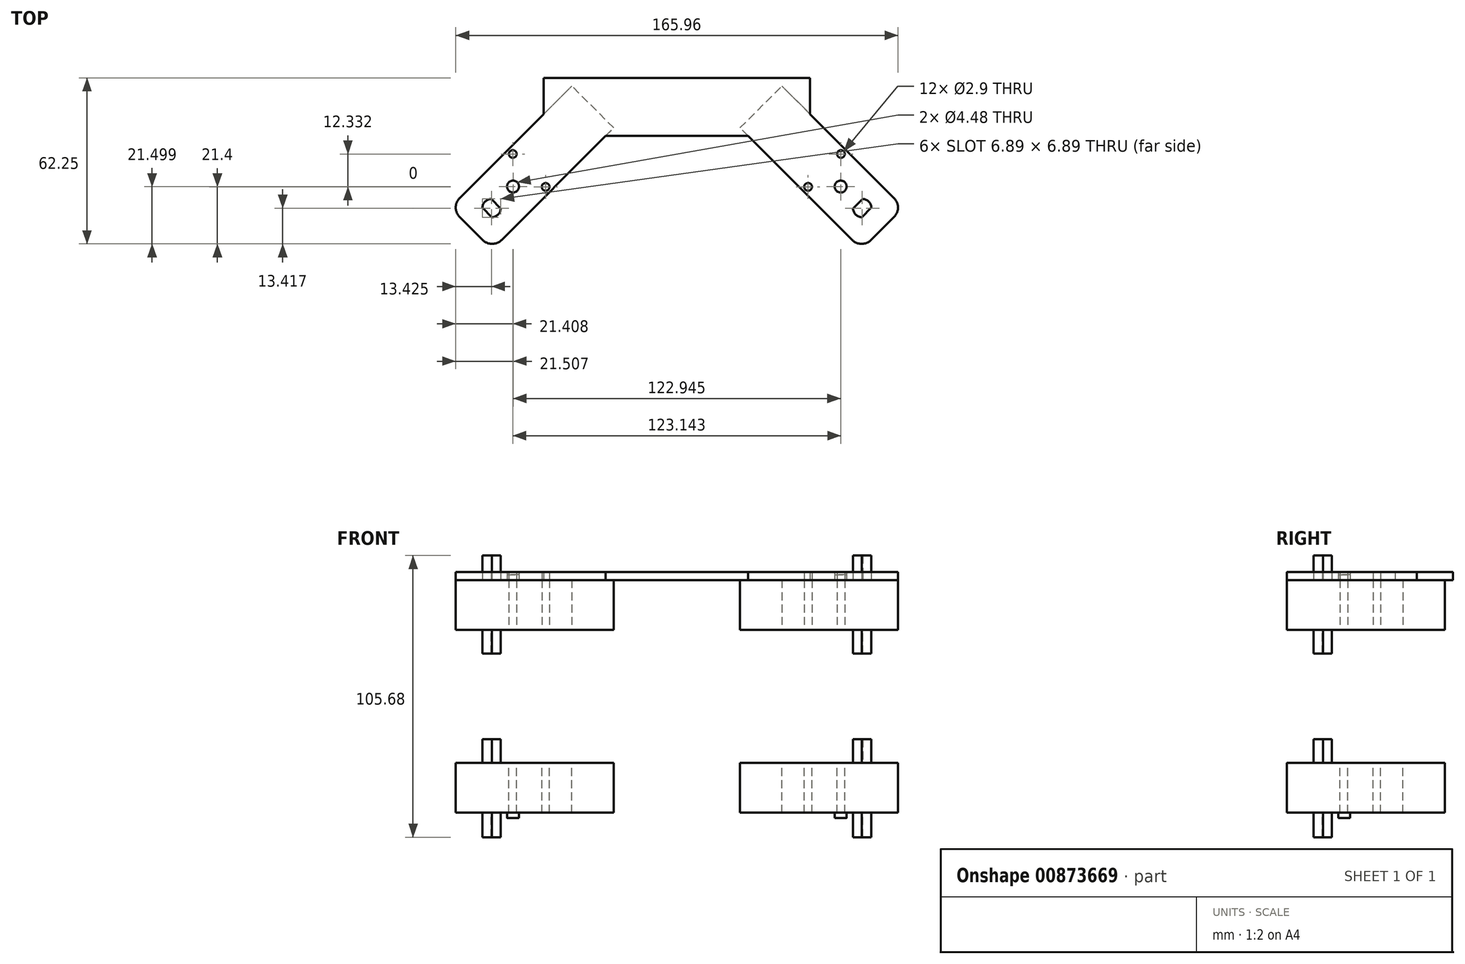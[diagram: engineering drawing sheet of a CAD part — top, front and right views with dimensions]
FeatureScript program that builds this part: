
annotation { "Feature Type Name" : "Feature", "Feature Type Description" : "" }
export const myFeature = defineFeature(function(context is Context, id is Id, definition is map)
    precondition{}
    {
        {
            var Q0;
            Q0=qCreatedBy(makeId("Top.planeOp"),FACE);
            var sketch = newSketch(context, id + "F0", { "sketchPlane" : qUnion([Q0])});
            skCircle(sketch, "E0", {"center": v(0, 0) * mm, "radius": 4.87 * mm});
            skCircle(sketch, "E1", {"center": v(-20.01, 8.72) * mm, "radius": 1.45 * mm});
            skCircle(sketch, "E2.MirrorC", {"center": v(-20.01, -8.72) * mm, "radius": 1.45 * mm});
            skLineSegment(sketch, "E3.bottom", {"start": v(5.8, -11.1) * mm, "end": v(-53.7, -11.11) * mm});
            skLineSegment(sketch, "E3.top", {"start": v(5.8, 11.1) * mm, "end": v(-53.71, 11.1) * mm});
            skLineSegment(sketch, "E3.left", {"start": v(10.8, -6.1) * mm, "end": v(10.8, 6.11) * mm});
            skLineSegment(sketch, "E3.right", {"start": v(-53.71, -11.11) * mm, "end": v(-53.71, 11.1) * mm});
            skPoint(sketch, "E3.middle", {"position": v(-21.46, 0) * mm});
            skCircle(sketch, "E4", {"center": v(-11.43, 0) * mm, "radius": 2.24 * mm});
            skPoint(sketch, "E5.visualSharp", {"position": v(10.8, 11.11) * mm});
            skArc(sketch, "E5.filletArc", {"start": v(10.8, 6.11) * mm, "mid": v(9.34, 9.65) * mm, "end": v(5.8, 11.1) * mm});
            skPoint(sketch, "E6.visualSharp", {"position": v(10.8, -11.1) * mm});
            skArc(sketch, "E6.filletArc", {"start": v(5.8, -11.1) * mm, "mid": v(9.34, -9.65) * mm, "end": v(10.8, -6.1) * mm});
            skCircle(sketch, "E7", {"center": v(0, 0) * mm, "radius": 3.42 * mm});
            skSolve(sketch);
        }
        {
            var Q0;
            Q0=makeQuery(id+"F0.imprint","IMPRINT",FACE,{"disambiguationData":[TD([[makeQuery(id+"F0.imprint","IMPRINT",EDGE,{"derivedFrom":sQuery(id+"F0.wireOp",EDGE,"E0")}),-1.0]])]});
            var Q1;
            Q1=makeQuery(id+"F0.imprint","IMPRINT",FACE,{"disambiguationData":[TD([[makeQuery(id+"F0.imprint","IMPRINT",EDGE,{"derivedFrom":sQuery(id+"F0.wireOp",EDGE,"E4")}),1.0]])]});
            var Q2;
            Q2=makeQuery(id+"F0.imprint","IMPRINT",FACE,{"disambiguationData":[TD([[makeQuery(id+"F0.imprint","IMPRINT",EDGE,{"derivedFrom":sQuery(id+"F0.wireOp",EDGE,"E7")}),1.0]])]});
            var Q3;
            Q3=makeQuery(id+"F0.imprint","IMPRINT",FACE,{"disambiguationData":[TD([[makeQuery(id+"F0.imprint","IMPRINT",EDGE,{"derivedFrom":sQuery(id+"F0.wireOp",EDGE,"E0")}),1.0]])]});
            extrude(context, id + "F1", {"entities" : qUnion([Q0, Q1, Q2, Q3]), "depth" : 18.64 * mm, "offsetDistance" : 25 * mm});
        }
        {
            var Q0;
            Q0=makeQuery(id+"F1.opExtrude","CAP_FACE",FACE,{"disambiguationData":[OSD([sQuery(id+"F0.wireOp",EDGE,"E1"),sQuery(id+"F0.wireOp",EDGE,"E2.MirrorC"),sQuery(id+"F0.wireOp",EDGE,"E3.bottom"),sQuery(id+"F0.wireOp",EDGE,"E3.top"),sQuery(id+"F0.wireOp",EDGE,"E3.left"),sQuery(id+"F0.wireOp",EDGE,"E3.right"),sQuery(id+"F0.wireOp",EDGE,"E5.filletArc"),sQuery(id+"F0.wireOp",EDGE,"E6.filletArc")])],"isStart":false});
            var sketch = newSketch(context, id + "F2", { "sketchPlane" : qUnion([Q0])});
            skArc(sketch, "E8", {"start": v(-2.33, -2.55) * mm, "mid": v(0, -3.45) * mm, "end": v(2.33, -2.55) * mm});
            skLineSegment(sketch, "E9.top", {"start": v(2.32, 2.55) * mm, "end": v(-2.33, 2.55) * mm});
            skLineSegment(sketch, "E9.left", {"start": v(2.33, -2.55) * mm, "end": v(2.33, 2.55) * mm});
            skLineSegment(sketch, "E9.right", {"start": v(-2.33, -2.55) * mm, "end": v(-2.33, 2.55) * mm});
            skArc(sketch, "E10.trimOffspring", {"start": v(2.33, 2.55) * mm, "mid": v(0, 3.45) * mm, "end": v(-2.33, 2.55) * mm});
            skSolve(sketch);
        }
        {
            var Q0;
            Q0 = qSketchRegion(id + "F2", true);
            extrude(context, id + "F3", {"entities" : qUnion([Q0]), "operationType" : NewBodyOperationType.ADD, "depth" : 9.2 * mm, "offsetDistance" : 25 * mm});
        }
        {
            var Q0;
            Q0=makeQuery(id+"F1.opExtrude","CAP_FACE",FACE,{"disambiguationData":[OSD([sQuery(id+"F0.wireOp",EDGE,"E1"),sQuery(id+"F0.wireOp",EDGE,"E2.MirrorC"),sQuery(id+"F0.wireOp",EDGE,"E3.bottom"),sQuery(id+"F0.wireOp",EDGE,"E3.top"),sQuery(id+"F0.wireOp",EDGE,"E3.left"),sQuery(id+"F0.wireOp",EDGE,"E3.right"),sQuery(id+"F0.wireOp",EDGE,"E5.filletArc"),sQuery(id+"F0.wireOp",EDGE,"E6.filletArc")])],"isStart":false});
            var sketch = newSketch(context, id + "F4", { "sketchPlane" : qUnion([Q0])});
            skCircle(sketch, "E11", {"center": v(-11.43, 0) * mm, "radius": 2.24 * mm});
            skSolve(sketch);
        }
        {
            var Q0;
            Q0 = qSketchRegion(id + "F4", true);
            extrude(context, id + "F5", {"entities" : qUnion([Q0]), "operationType" : NewBodyOperationType.ADD, "depth" : 2 * mm, "offsetDistance" : 25 * mm});
        }
        {
            var Q0;
            Q0=makeQuery(id+"F0.imprint","IMPRINT",FACE,{"disambiguationData":[TD([[makeQuery(id+"F0.imprint","IMPRINT",EDGE,{"derivedFrom":sQuery(id+"F0.wireOp",EDGE,"E0")}),-1.0]])]});
            var sketch = newSketch(context, id + "F6", { "sketchPlane" : qUnion([Q0])});
            skCircle(sketch, "E12", {"center": v(0, 0) * mm, "radius": 3.45 * mm});
            skLineSegment(sketch, "E13.bottom", {"start": v(-2.33, -2.55) * mm, "end": v(2.33, -2.55) * mm});
            skLineSegment(sketch, "E13.top", {"start": v(-2.33, 2.55) * mm, "end": v(2.33, 2.55) * mm});
            skLineSegment(sketch, "E13.left", {"start": v(-2.33, -2.55) * mm, "end": v(-2.33, 2.55) * mm});
            skLineSegment(sketch, "E13.right", {"start": v(2.33, -2.55) * mm, "end": v(2.33, 2.55) * mm});
            skSolve(sketch);
        }
        {
            var Q0;
            {var subQ0=sQuery(id+"F6.wireOp",EDGE,"E13.top");Q0=makeQuery(id+"F6.imprint","IMPRINT",FACE,{"disambiguationData":[TD([[makeQuery(id+"F6.imprint","IMPRINT",EDGE,{"derivedFrom":subQ0}),1.0]])]});}
            var Q1;
            {var subQ0=sQuery(id+"F6.wireOp",EDGE,"E13.bottom");Q1=makeQuery(id+"F6.imprint","IMPRINT",FACE,{"disambiguationData":[TD([[makeQuery(id+"F6.imprint","IMPRINT",EDGE,{"derivedFrom":subQ0}),-1.0]])]});}
            var Q2;
            Q2=makeQuery(id+"F6.imprint","IMPRINT",FACE,{"disambiguationData":[TD([[makeQuery(id+"F6.imprint","IMPRINT",EDGE,{"derivedFrom":sQuery(id+"F6.wireOp",EDGE,"E13.bottom")}),1.0]])]});
            extrude(context, id + "F7", {"entities" : qUnion([Q0, Q1, Q2]), "operationType" : NewBodyOperationType.ADD, "oppositeDirection" : true, "depth" : 8.93 * mm, "offsetDistance" : 25 * mm});
        }
        {
            var Q0;
            Q0=makeQuery(id+"F1.opExtrude","SWEPT_BODY",BODY,{"disambiguationData":[OSD([sQuery(id+"F0.wireOp",EDGE,"E1"),sQuery(id+"F0.wireOp",EDGE,"E2.MirrorC"),sQuery(id+"F0.wireOp",EDGE,"E3.bottom"),sQuery(id+"F0.wireOp",EDGE,"E3.top"),sQuery(id+"F0.wireOp",EDGE,"E3.left"),sQuery(id+"F0.wireOp",EDGE,"E3.right"),sQuery(id+"F0.wireOp",EDGE,"E5.filletArc"),sQuery(id+"F0.wireOp",EDGE,"E6.filletArc")])]});
            var Q1;
            Q1=makeQuery(id+"F1.opExtrude","SWEPT_EDGE",EDGE,{"disambiguationData":[OSD([sQuery(id+"F0.wireOp",EDGE,"E3.bottom"),sQuery(id+"F0.wireOp",EDGE,"E6.filletArc")])]});
            transform(context, id + "F8", {"entities" : qUnion([Q0]), "transformType" : TransformType.ROTATION, "transformAxis" : qUnion([Q1]), "angle" : 45 * degree, "makeCopy" : false});
        }
        {
            var Q0;
            Q0=qCreatedBy(makeId("Right.planeOp"),FACE);
            cPlane(context, id + "F9", {"entities" : qUnion([Q0]), "cplaneType" : CPlaneType.OFFSET, "offset" : 60 * mm, "oppositeDirection" : true, "width" : 150 * mm, "height" : 150 * mm});
        }
        {
            var Q0;
            Q0=makeQuery(id+"F1.opExtrude","SWEPT_BODY",BODY,{"disambiguationData":[OSD([sQuery(id+"F0.wireOp",EDGE,"E1"),sQuery(id+"F0.wireOp",EDGE,"E2.MirrorC"),sQuery(id+"F0.wireOp",EDGE,"E3.bottom"),sQuery(id+"F0.wireOp",EDGE,"E3.top"),sQuery(id+"F0.wireOp",EDGE,"E3.left"),sQuery(id+"F0.wireOp",EDGE,"E3.right"),sQuery(id+"F0.wireOp",EDGE,"E5.filletArc"),sQuery(id+"F0.wireOp",EDGE,"E6.filletArc")])]});
            var Q1;
            Q1=qCreatedBy(id+"F9.planeOp",FACE);
            mirror(context, id + "F10", {"entities" : qUnion([Q0]), "mirrorPlane" : qUnion([Q1])});
        }
        {
            var Q0;
            Q0=qCreatedBy(makeId("Top.planeOp"),FACE);
            cPlane(context, id + "F11", {"entities" : qUnion([Q0]), "cplaneType" : CPlaneType.OFFSET, "offset" : 25 * mm, "oppositeDirection" : true, "width" : 150 * mm, "height" : 150 * mm});
        }
        {
            var Q0;
            Q0=makeQuery(id+"F1.opExtrude","SWEPT_BODY",BODY,{"disambiguationData":[OSD([sQuery(id+"F0.wireOp",EDGE,"E1"),sQuery(id+"F0.wireOp",EDGE,"E2.MirrorC"),sQuery(id+"F0.wireOp",EDGE,"E3.bottom"),sQuery(id+"F0.wireOp",EDGE,"E3.top"),sQuery(id+"F0.wireOp",EDGE,"E3.left"),sQuery(id+"F0.wireOp",EDGE,"E3.right"),sQuery(id+"F0.wireOp",EDGE,"E5.filletArc"),sQuery(id+"F0.wireOp",EDGE,"E6.filletArc")])]});
            var Q1;
            Q1=makeQuery(id+"F10.opPattern","COPY",BODY,{"derivedFrom":makeQuery(id+"F1.opExtrude","SWEPT_BODY",BODY,{"disambiguationData":[OSD([sQuery(id+"F0.wireOp",EDGE,"E1"),sQuery(id+"F0.wireOp",EDGE,"E2.MirrorC"),sQuery(id+"F0.wireOp",EDGE,"E3.bottom"),sQuery(id+"F0.wireOp",EDGE,"E3.top"),sQuery(id+"F0.wireOp",EDGE,"E3.left"),sQuery(id+"F0.wireOp",EDGE,"E3.right"),sQuery(id+"F0.wireOp",EDGE,"E5.filletArc"),sQuery(id+"F0.wireOp",EDGE,"E6.filletArc")])]}),"instanceName":"1"});
            var Q2;
            Q2=qCreatedBy(id+"F11.planeOp",FACE);
            mirror(context, id + "F12", {"entities" : qUnion([Q0, Q1]), "mirrorPlane" : qUnion([Q2])});
        }
        {
            var Q0;
            Q0=qCreatedBy(makeId("Top.planeOp"),FACE);
            cPlane(context, id + "F13", {"entities" : qUnion([Q0]), "cplaneType" : CPlaneType.OFFSET, "offset" : 18.6 * mm, "width" : 150 * mm, "height" : 150 * mm});
        }
        {
            var Q0;
            Q0=qCreatedBy(id+"F13.planeOp",FACE);
            var sketch = newSketch(context, id + "F14", { "sketchPlane" : qUnion([Q0])});
            skLineSegment(sketch, "E14", {"start": v(-142.98, 1.07) * mm, "end": v(22.98, 1.07) * mm});
            skLineSegment(sketch, "E15.bottom", {"start": v(22.98, 49.68) * mm, "end": v(-142.98, 49.68) * mm});
            skLineSegment(sketch, "E15.top", {"start": v(22.98, -47.55) * mm, "end": v(-142.98, -47.55) * mm});
            skLineSegment(sketch, "E15.left", {"start": v(22.98, 49.68) * mm, "end": v(22.98, -47.55) * mm});
            skLineSegment(sketch, "E15.right", {"start": v(-142.98, 49.68) * mm, "end": v(-142.98, -47.55) * mm});
            skPoint(sketch, "E15.middle", {"position": v(-60, 1.07) * mm});
            skLineSegment(sketch, "E16", {"start": v(-142.98, -12.57) * mm, "end": v(22.98, -12.57) * mm});
            skLineSegment(sketch, "E17.0", {"start": v(-141.51, 4.6) * mm, "end": v(-99.43, 46.68) * mm});
            skLineSegment(sketch, "E17.1", {"start": v(-132.87, -11.1) * mm, "end": v(-141.51, -2.47) * mm});
            skLineSegment(sketch, "E17.2", {"start": v(-125.8, -11.11) * mm, "end": v(-83.72, 30.97) * mm});
            skLineSegment(sketch, "E17.3", {"start": v(-83.72, 30.97) * mm, "end": v(-99.43, 46.68) * mm});
            skLineSegment(sketch, "E18", {"start": v(-60, -12.57) * mm, "end": v(-60, 49.68) * mm, "construction": true});
            skLineSegment(sketch, "E19.MirrorCS", {"start": v(5.8, -11.1) * mm, "end": v(-36.28, 30.97) * mm});
            skLineSegment(sketch, "E20.MirrorCS", {"start": v(-36.28, 30.97) * mm, "end": v(-20.57, 46.68) * mm});
            skLineSegment(sketch, "E21.MirrorCS", {"start": v(21.51, 4.6) * mm, "end": v(-20.57, 46.68) * mm});
            skLineSegment(sketch, "E22.MirrorCS", {"start": v(12.87, -11.1) * mm, "end": v(21.51, -2.47) * mm});
            skPoint(sketch, "E23.visualSharp", {"position": v(9.34, -14.65) * mm});
            skArc(sketch, "E23.filletArc", {"start": v(5.8, -11.1) * mm, "mid": v(9.34, -12.57) * mm, "end": v(12.87, -11.1) * mm});
            skPoint(sketch, "E24.visualSharp", {"position": v(25.05, 1.07) * mm});
            skArc(sketch, "E24.filletArc", {"start": v(21.51, -2.47) * mm, "mid": v(22.98, 1.07) * mm, "end": v(21.51, 4.6) * mm});
            skPoint(sketch, "E25.visualSharp", {"position": v(-129.34, -14.65) * mm});
            skArc(sketch, "E25.filletArc", {"start": v(-132.87, -11.11) * mm, "mid": v(-129.34, -12.57) * mm, "end": v(-125.8, -11.11) * mm});
            skPoint(sketch, "E26.visualSharp", {"position": v(-145.05, 1.07) * mm});
            skArc(sketch, "E26.filletArc", {"start": v(-141.51, 4.6) * mm, "mid": v(-142.98, 1.07) * mm, "end": v(-141.51, -2.47) * mm});
            skLineSegment(sketch, "E27", {"start": v(-33.28, 27.97) * mm, "end": v(-86.72, 27.97) * mm});
            skLineSegment(sketch, "E28.bottom", {"start": v(-10, 49.68) * mm, "end": v(-110, 49.68) * mm});
            skLineSegment(sketch, "E28.top", {"start": v(-10, 43.68) * mm, "end": v(-110, 43.68) * mm});
            skLineSegment(sketch, "E28.left", {"start": v(-10, 49.68) * mm, "end": v(-10, 43.68) * mm});
            skLineSegment(sketch, "E28.right", {"start": v(-110, 49.68) * mm, "end": v(-110, 43.68) * mm});
            skPoint(sketch, "E28.middle", {"position": v(-60, 46.68) * mm});
            skLineSegment(sketch, "E29", {"start": v(-110, 43.68) * mm, "end": v(-110, 36.11) * mm});
            skLineSegment(sketch, "E30.MirrorCS", {"start": v(-10, 43.68) * mm, "end": v(-10, 36.11) * mm});
            skSolve(sketch);
        }
        {
            var Q0;
            Q0=makeQuery(id+"F10.opPattern","COPY",FACE,{"derivedFrom":makeQuery(id+"F1.opExtrude","CAP_FACE",FACE,{"disambiguationData":[OSD([sQuery(id+"F0.wireOp",EDGE,"E1"),sQuery(id+"F0.wireOp",EDGE,"E2.MirrorC"),sQuery(id+"F0.wireOp",EDGE,"E3.bottom"),sQuery(id+"F0.wireOp",EDGE,"E3.top"),sQuery(id+"F0.wireOp",EDGE,"E3.left"),sQuery(id+"F0.wireOp",EDGE,"E3.right"),sQuery(id+"F0.wireOp",EDGE,"E5.filletArc"),sQuery(id+"F0.wireOp",EDGE,"E6.filletArc")])],"isStart":false}),"instanceName":"1"});
            var Q1;
            Q1=makeQuery(id+"F1.opExtrude","CAP_FACE",FACE,{"disambiguationData":[OSD([sQuery(id+"F0.wireOp",EDGE,"E1"),sQuery(id+"F0.wireOp",EDGE,"E2.MirrorC"),sQuery(id+"F0.wireOp",EDGE,"E3.bottom"),sQuery(id+"F0.wireOp",EDGE,"E3.top"),sQuery(id+"F0.wireOp",EDGE,"E3.left"),sQuery(id+"F0.wireOp",EDGE,"E3.right"),sQuery(id+"F0.wireOp",EDGE,"E5.filletArc"),sQuery(id+"F0.wireOp",EDGE,"E6.filletArc")])],"isStart":false});
            var Q2;
            {var subQ9=sQuery(id+"F14.wireOp",EDGE,"E27");Q2=makeQuery(id+"F14.imprint","IMPRINT",FACE,{"disambiguationData":[TD([[makeQuery(id+"F14.imprint","IMPRINT",EDGE,{"derivedFrom":subQ9}),-1.0]])]});}
            var Q3;
            {var subQ10=sQuery(id+"F14.wireOp",EDGE,"E28.left");Q3=makeQuery(id+"F14.imprint","IMPRINT",FACE,{"disambiguationData":[TD([[makeQuery(id+"F14.imprint","IMPRINT",EDGE,{"derivedFrom":subQ10}),-1.0]])]});}
            var Q4;
            {var subQ0=sQuery(id+"F14.wireOp",EDGE,"E30.MirrorCS");Q4=makeQuery(id+"F14.imprint","IMPRINT",FACE,{"disambiguationData":[TD([[makeQuery(id+"F14.imprint","IMPRINT",EDGE,{"derivedFrom":subQ0}),-1.0]])]});}
            var Q5;
            {var subQ0=sQuery(id+"F14.wireOp",EDGE,"E29");Q5=makeQuery(id+"F14.imprint","IMPRINT",FACE,{"disambiguationData":[TD([[makeQuery(id+"F14.imprint","IMPRINT",EDGE,{"derivedFrom":subQ0}),1.0]])]});}
            extrude(context, id + "F15", {"entities" : qUnion([Q0, Q1, Q2, Q3, Q4, Q5]), "depth" : 3 * mm, "offsetDistance" : 25 * mm});
        }
        {
            var Q0;
            Q0=makeQuery(id+"F15.opExtrude","CAP_FACE",FACE,{"disambiguationData":[OSD([sQuery(id+"F14.wireOp",EDGE,"E15.bottom"),sQuery(id+"F14.wireOp",EDGE,"E17.0"),sQuery(id+"F14.wireOp",EDGE,"E17.2"),sQuery(id+"F14.wireOp",EDGE,"E17.3"),sQuery(id+"F14.wireOp",EDGE,"E19.MirrorCS"),sQuery(id+"F14.wireOp",EDGE,"E20.MirrorCS"),sQuery(id+"F14.wireOp",EDGE,"E21.MirrorCS"),sQuery(id+"F14.wireOp",EDGE,"E27"),sQuery(id+"F14.wireOp",EDGE,"E28.left"),sQuery(id+"F14.wireOp",EDGE,"E28.right"),sQuery(id+"F14.wireOp",EDGE,"E29"),sQuery(id+"F14.wireOp",EDGE,"E30.MirrorCS")])],"isStart":true});
            extrude(context, id + "F16", {"entities" : qUnion([Q0]), "operationType" : NewBodyOperationType.REMOVE, "oppositeDirection" : true, "depth" : 0.04 * mm, "offsetDistance" : 25 * mm});
        }
        {
            var Q0;
            Q0=makeQuery(id+"F15.opExtrude","CAP_FACE",FACE,{"disambiguationData":[OSD([sQuery(id+"F14.wireOp",EDGE,"E15.bottom"),sQuery(id+"F14.wireOp",EDGE,"E17.0"),sQuery(id+"F14.wireOp",EDGE,"E17.2"),sQuery(id+"F14.wireOp",EDGE,"E17.3"),sQuery(id+"F14.wireOp",EDGE,"E19.MirrorCS"),sQuery(id+"F14.wireOp",EDGE,"E20.MirrorCS"),sQuery(id+"F14.wireOp",EDGE,"E21.MirrorCS"),sQuery(id+"F14.wireOp",EDGE,"E27"),sQuery(id+"F14.wireOp",EDGE,"E28.left"),sQuery(id+"F14.wireOp",EDGE,"E28.right"),sQuery(id+"F14.wireOp",EDGE,"E29"),sQuery(id+"F14.wireOp",EDGE,"E30.MirrorCS")])],"isStart":false});
            extrude(context, id + "F17", {"entities" : qUnion([Q0]), "operationType" : NewBodyOperationType.ADD, "depth" : 0.04 * mm, "offsetDistance" : 25 * mm});
        }
    });
